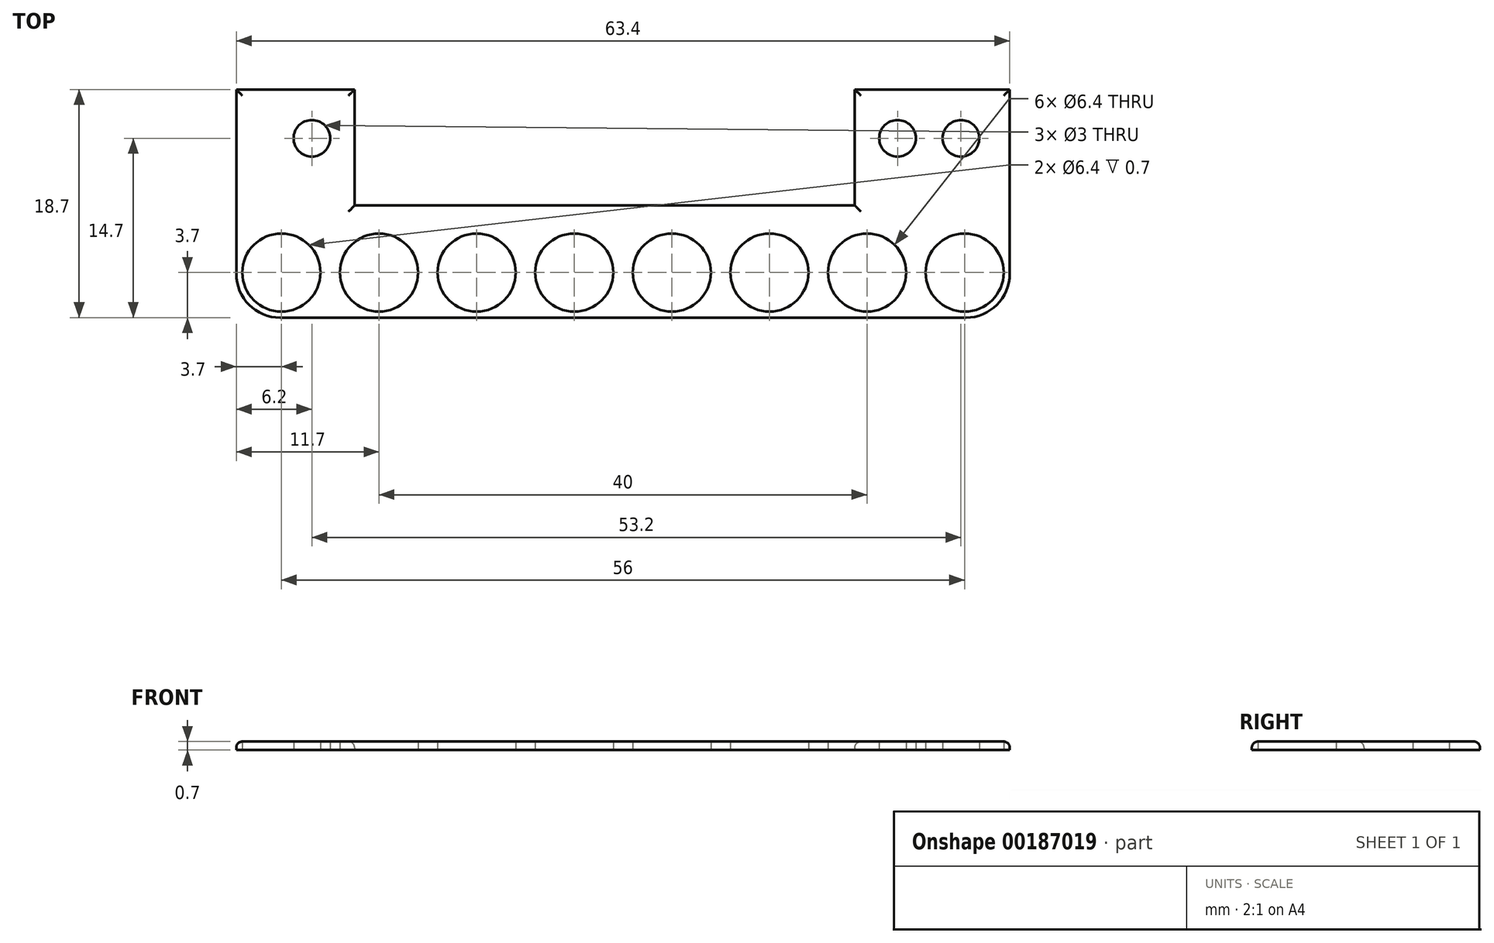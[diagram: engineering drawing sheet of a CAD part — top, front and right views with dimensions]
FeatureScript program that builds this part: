
annotation { "Feature Type Name" : "Feature", "Feature Type Description" : "" }
export const myFeature = defineFeature(function(context is Context, id is Id, definition is map)
    precondition{}
    {
        {
            var Q0;
            Q0=qCreatedBy(makeId("Top.planeOp"),FACE);
            var sketch = newSketch(context, id + "F0", { "sketchPlane" : qUnion([Q0])});
            skLineSegment(sketch, "E0", {"start": v(-31.7, 18.7) * mm, "end": v(-22, 18.7) * mm});
            skLineSegment(sketch, "E1", {"start": v(-22, 18.7) * mm, "end": v(-22, 9.2) * mm});
            skLineSegment(sketch, "E2", {"start": v(-22, 9.2) * mm, "end": v(19, 9.2) * mm});
            skLineSegment(sketch, "E3", {"start": v(19, 9.2) * mm, "end": v(19, 18.7) * mm});
            skLineSegment(sketch, "E4", {"start": v(19, 18.7) * mm, "end": v(31.7, 18.7) * mm});
            skLineSegment(sketch, "E5", {"start": v(31.7, 18.7) * mm, "end": v(31.7, 0) * mm});
            skLineSegment(sketch, "E6", {"start": v(31.7, 0) * mm, "end": v(-31.7, 0) * mm});
            skLineSegment(sketch, "E7", {"start": v(-31.7, 0) * mm, "end": v(-31.7, 18.7) * mm});
            skCircle(sketch, "E8", {"center": v(-25.5, 14.7) * mm, "radius": 1.5 * mm});
            skCircle(sketch, "E9", {"center": v(22.5, 14.7) * mm, "radius": 1.5 * mm});
            skCircle(sketch, "E10", {"center": v(-28, 3.7) * mm, "radius": 3.2 * mm});
            skCircle(sketch, "E11", {"center": v(4, 3.7) * mm, "radius": 3.2 * mm});
            skCircle(sketch, "E12", {"center": v(-12, 3.7) * mm, "radius": 3.2 * mm});
            skCircle(sketch, "E13", {"center": v(-4, 3.7) * mm, "radius": 3.2 * mm});
            skLineSegment(sketch, "E14.top", {"start": v(-10.35, 0) * mm, "end": v(-18.35, 0) * mm});
            skCircle(sketch, "E15", {"center": v(-20, 3.7) * mm, "radius": 3.2 * mm});
            skCircle(sketch, "E16", {"center": v(12, 3.7) * mm, "radius": 3.2 * mm});
            skCircle(sketch, "E17", {"center": v(20, 3.7) * mm, "radius": 3.2 * mm});
            skCircle(sketch, "E18", {"center": v(28, 3.7) * mm, "radius": 3.2 * mm});
            skCircle(sketch, "E19", {"center": v(27.7, 14.7) * mm, "radius": 1.5 * mm});
            skSolve(sketch);
        }
        {
            var Q0;
            Q0=makeQuery(id+"F0.imprint","IMPRINT",FACE,{"disambiguationData":[TD([[makeQuery(id+"F0.imprint","IMPRINT",EDGE,{"derivedFrom":sQuery(id+"F0.wireOp",EDGE,"E0")}),-1.0]])]});
            extrude(context, id + "F1", {"entities" : qUnion([Q0]), "depth" : 0.7 * mm});
        }
        {
            var Q0;
            Q0=makeQuery(id+"F1.opExtrude","CAP_EDGE",EDGE,{"disambiguationData":[OSD([sQuery(id+"F0.wireOp",EDGE,"E6")])],"isStart":false});
            var Q1;
            Q1=makeQuery(id+"F1.opExtrude","CAP_EDGE",EDGE,{"disambiguationData":[OSD([sQuery(id+"F0.wireOp",EDGE,"E7"),sQuery(id+"F0.wireOp",EDGE,"gDoAqS5J-GwKx-NIl1-ceZj-vuHMme4C13Uk.right")])],"isStart":false});
            var Q2;
            Q2=makeQuery(id+"F1.opExtrude","CAP_EDGE",EDGE,{"disambiguationData":[OSD([sQuery(id+"F0.wireOp",EDGE,"E0")])],"isStart":false});
            var Q3;
            Q3=makeQuery(id+"F1.opExtrude","CAP_EDGE",EDGE,{"disambiguationData":[OSD([sQuery(id+"F0.wireOp",EDGE,"E1")])],"isStart":false});
            var Q4;
            Q4=makeQuery(id+"F1.opExtrude","CAP_EDGE",EDGE,{"disambiguationData":[OSD([sQuery(id+"F0.wireOp",EDGE,"E2")])],"isStart":false});
            var Q5;
            Q5=makeQuery(id+"F1.opExtrude","CAP_EDGE",EDGE,{"disambiguationData":[OSD([sQuery(id+"F0.wireOp",EDGE,"E3")])],"isStart":false});
            var Q6;
            Q6=makeQuery(id+"F1.opExtrude","CAP_EDGE",EDGE,{"disambiguationData":[OSD([sQuery(id+"F0.wireOp",EDGE,"E4"),sQuery(id+"F0.wireOp",EDGE,"y1poqJQj-ZdzA-tnpm-zgBr-kg1aAtWxKc9v.bottom")])],"isStart":false});
            var Q7;
            Q7=makeQuery(id+"F1.opExtrude","CAP_EDGE",EDGE,{"disambiguationData":[OSD([sQuery(id+"F0.wireOp",EDGE,"E5")])],"isStart":false});
            fillet(context, id + "F2", {"entities" : qUnion([Q0, Q1, Q2, Q3, Q4, Q5, Q6, Q7]), "radius" : 0.5 * mm, "tangentPropagation" : true, "allowEdgeOverflow" : false});
        }
        {
            var Q0;
            Q0=makeQuery(id+"F1.opExtrude","SWEPT_EDGE",EDGE,{"disambiguationData":[OSD([sQuery(id+"F0.wireOp",EDGE,"E6"),sQuery(id+"F0.wireOp",EDGE,"E7")])]});
            var Q1;
            Q1=makeQuery(id+"F2.opFillet","BLEND_EDGE",EDGE,{"blendedFrom":[makeQuery(id+"F1.opExtrude","CAP_EDGE",EDGE,{"disambiguationData":[OSD([sQuery(id+"F0.wireOp",EDGE,"E6"),sQuery(id+"F0.wireOp",EDGE,"E14.top")])],"isStart":false}),makeQuery(id+"F1.opExtrude","CAP_EDGE",EDGE,{"disambiguationData":[OSD([sQuery(id+"F0.wireOp",EDGE,"E7")])],"isStart":false})],"blendedInto":[]});
            var Q2;
            Q2=makeQuery(id+"F1.opExtrude","SWEPT_EDGE",EDGE,{"disambiguationData":[OSD([sQuery(id+"F0.wireOp",EDGE,"E5"),sQuery(id+"F0.wireOp",EDGE,"E6")])]});
            var Q3;
            Q3=makeQuery(id+"F2.opFillet","BLEND_EDGE",EDGE,{"blendedFrom":[makeQuery(id+"F1.opExtrude","CAP_EDGE",EDGE,{"disambiguationData":[OSD([sQuery(id+"F0.wireOp",EDGE,"E5")])],"isStart":false}),makeQuery(id+"F1.opExtrude","CAP_EDGE",EDGE,{"disambiguationData":[OSD([sQuery(id+"F0.wireOp",EDGE,"E6"),sQuery(id+"F0.wireOp",EDGE,"E14.top")])],"isStart":false})],"blendedInto":[]});
            fillet(context, id + "F3", {"entities" : qUnion([Q0, Q1, Q2, Q3]), "radius" : 3.6 * mm, "tangentPropagation" : true, "allowEdgeOverflow" : false});
        }
    });
